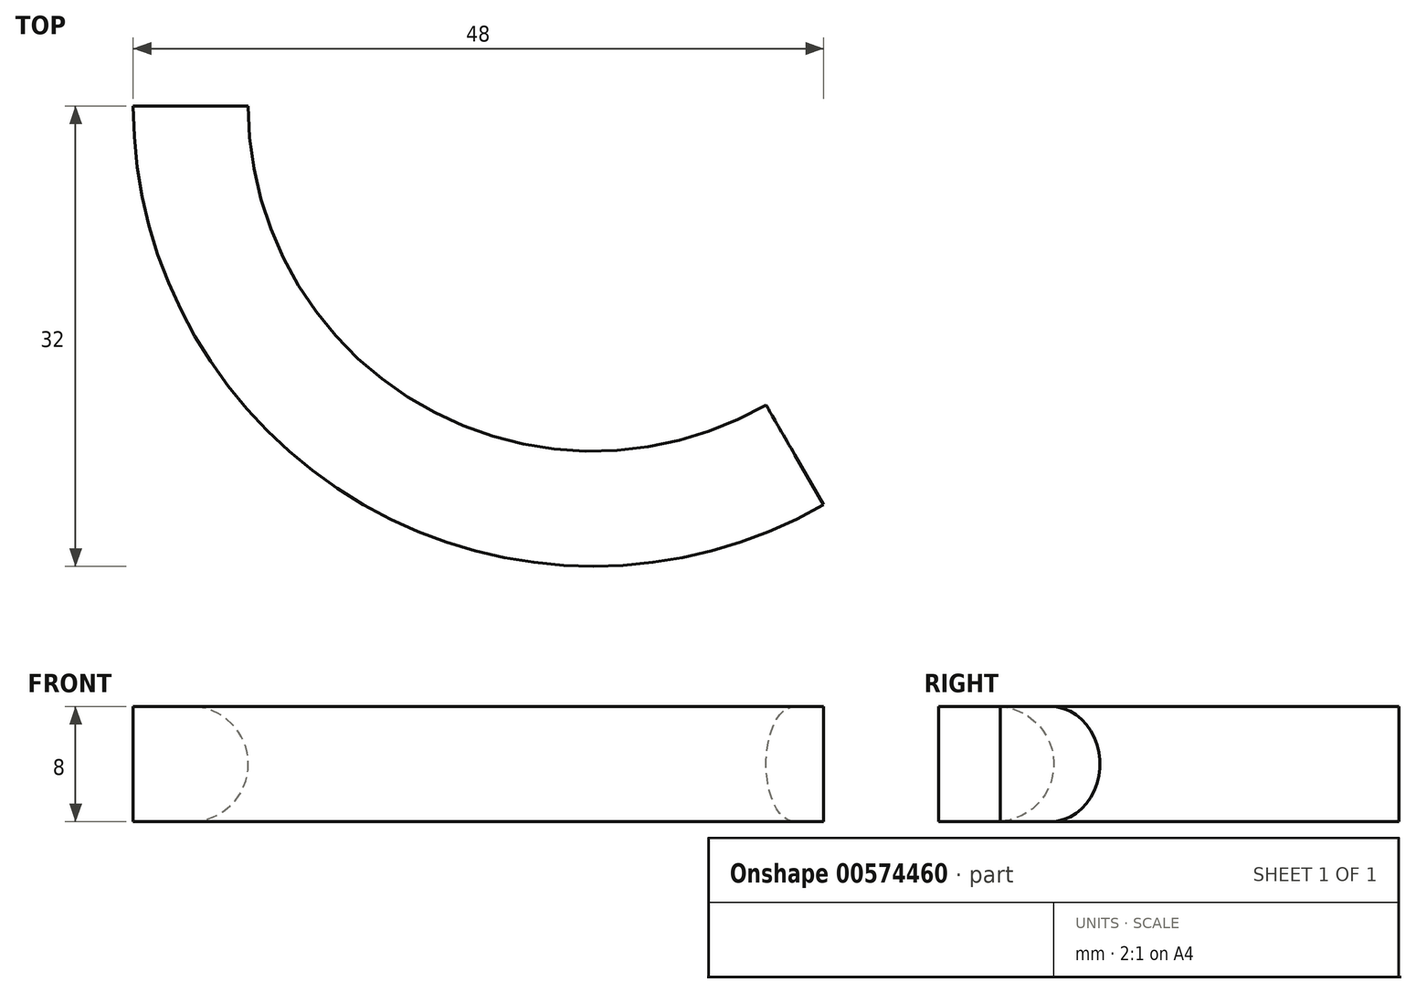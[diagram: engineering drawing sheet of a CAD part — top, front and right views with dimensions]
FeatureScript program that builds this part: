
annotation { "Feature Type Name" : "Feature", "Feature Type Description" : "" }
export const myFeature = defineFeature(function(context is Context, id is Id, definition is map)
    precondition{}
    {
        {
            var Q0;
            Q0=qCreatedBy(makeId("Front.planeOp"),FACE);
            var sketch = newSketch(context, id + "F0", { "sketchPlane" : qUnion([Q0])});
            skLineSegment(sketch, "E0.bottom", {"start": v(5.2, -2.33) * mm, "end": v(1.2, -2.33) * mm});
            skLineSegment(sketch, "E0.top", {"start": v(5.2, 5.67) * mm, "end": v(1.2, 5.67) * mm});
            skLineSegment(sketch, "E0.left", {"start": v(5.2, -2.33) * mm, "end": v(5.2, 5.67) * mm});
            skLineSegment(sketch, "E0.right", {"start": v(1.2, -2.33) * mm, "end": v(1.2, 5.67) * mm});
            skArc(sketch, "E1", {"start": v(5.2, -2.33) * mm, "mid": v(9.2, 1.67) * mm, "end": v(5.2, 5.67) * mm});
            skLineSegment(sketch, "E2", {"start": v(5.2, -2.33) * mm, "end": v(33.2, -2.33) * mm});
            skLineSegment(sketch, "E3", {"start": v(33.2, -2.33) * mm, "end": v(33.2, 6) * mm});
            skSolve(sketch);
        }
        {
            var Q0;
            Q0=qSketchRegion(id+"F0",true);
            var Q1;
            Q1=sQuery(id+"F0.wireOp",EDGE,"E3");
            revolve(context, id + "F1", {"surfaceOperationType" : NewSurfaceOperationType.NEW, "entities" : qUnion([Q0]), "axis" : qUnion([Q1]), "revolveType" : RevolveType.ONE_DIRECTION, "angle" : 120 * degree});
        }
    });
